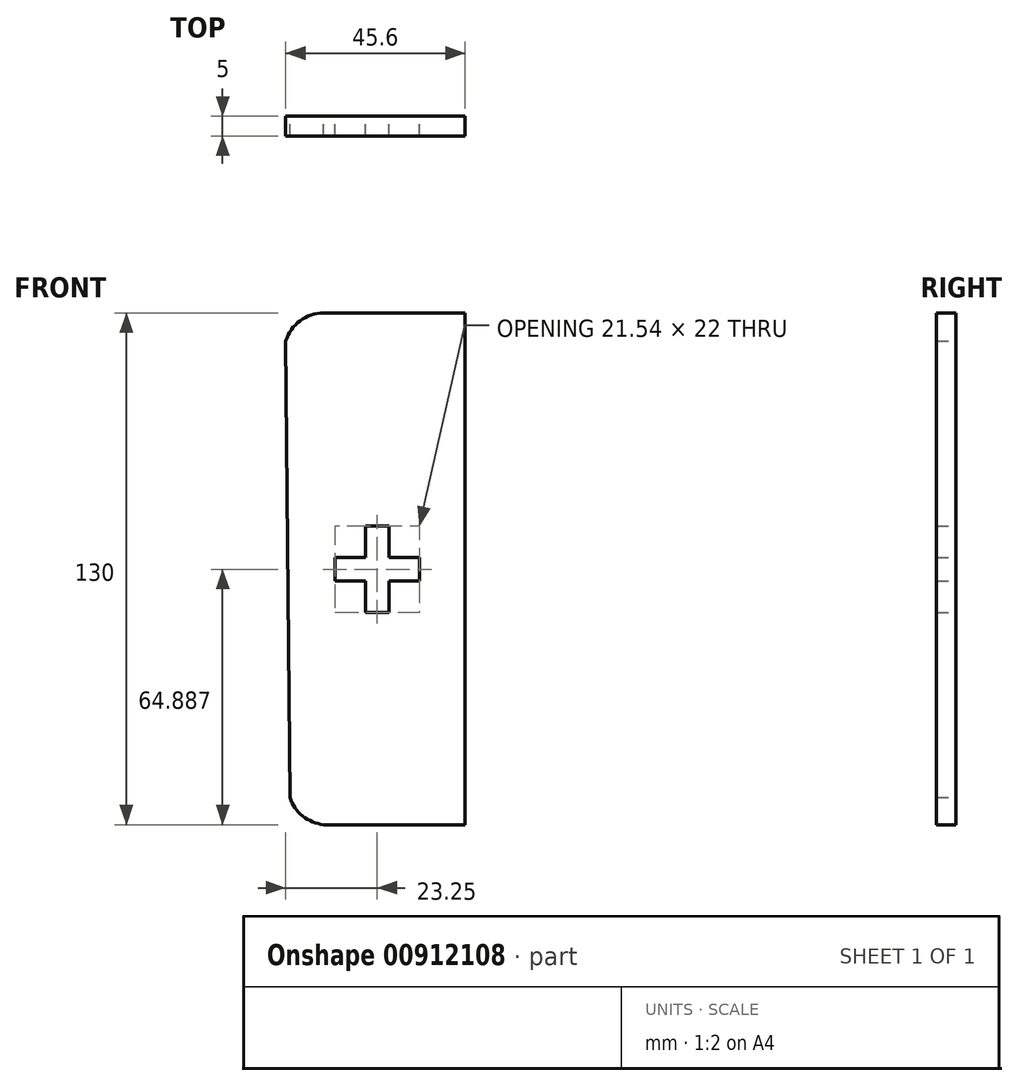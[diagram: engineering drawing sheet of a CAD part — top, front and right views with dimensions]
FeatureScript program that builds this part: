
annotation { "Feature Type Name" : "Feature", "Feature Type Description" : "" }
export const myFeature = defineFeature(function(context is Context, id is Id, definition is map)
    precondition{}
    {
        {
            var Q0;
            Q0=qCreatedBy(makeId("Front.planeOp"),FACE);
            var sketch = newSketch(context, id + "F0", { "sketchPlane" : qUnion([Q0])});
            skLineSegment(sketch, "E0", {"start": v(8.34, 35.26) * mm, "end": v(-27.63, 35.26) * mm});
            skArc(sketch, "E1", {"start": v(-27.63, 35.26) * mm, "mid": v(-33.63, 33.28) * mm, "end": v(-37.26, 28.1) * mm});
            skLineSegment(sketch, "E2", {"start": v(-27.63, -94.74) * mm, "end": v(8.34, -94.74) * mm});
            skArc(sketch, "E3", {"start": v(-36.18, -87.81) * mm, "mid": v(-32.94, -92.55) * mm, "end": v(-27.63, -94.74) * mm});
            skLineSegment(sketch, "E4", {"start": v(-37.26, 28.1) * mm, "end": v(-36.18, -87.81) * mm});
            skLineSegment(sketch, "E5", {"start": v(8.34, 35.26) * mm, "end": v(8.34, -94.74) * mm});
            skPoint(sketch, "E6.endSnap0", {"position": v(8.34, -29.74) * mm});
            skLineSegment(sketch, "E7.top", {"start": v(-17, -18.85) * mm, "end": v(-11, -18.85) * mm});
            skLineSegment(sketch, "E7.left", {"start": v(-17, -26.85) * mm, "end": v(-17, -18.85) * mm});
            skLineSegment(sketch, "E7.right", {"start": v(-11, -26.85) * mm, "end": v(-11, -18.85) * mm});
            skLineSegment(sketch, "E8.top", {"start": v(-11, -40.85) * mm, "end": v(-17, -40.85) * mm});
            skLineSegment(sketch, "E8.left", {"start": v(-11, -32.85) * mm, "end": v(-11, -40.85) * mm});
            skLineSegment(sketch, "E8.right", {"start": v(-17, -32.85) * mm, "end": v(-17, -40.85) * mm});
            skPoint(sketch, "E9", {"position": v(-11, -26.85) * mm});
            skPoint(sketch, "E10", {"position": v(-11, -32.85) * mm});
            skLineSegment(sketch, "E11.bottom", {"start": v(-11, -26.85) * mm, "end": v(-3.24, -26.85) * mm});
            skLineSegment(sketch, "E11.top", {"start": v(-11, -32.85) * mm, "end": v(-3.24, -32.85) * mm});
            skLineSegment(sketch, "E11.right", {"start": v(-3.24, -26.85) * mm, "end": v(-3.24, -32.85) * mm});
            skLineSegment(sketch, "E12.bottom", {"start": v(-17, -32.85) * mm, "end": v(-24.78, -32.85) * mm});
            skLineSegment(sketch, "E12.top", {"start": v(-17, -26.85) * mm, "end": v(-24.78, -26.85) * mm});
            skLineSegment(sketch, "E12.right", {"start": v(-24.78, -32.85) * mm, "end": v(-24.78, -26.85) * mm});
            skPoint(sketch, "E13.trimOffspring.end.orphan", {"position": v(8.34, -28.3) * mm});
            skPoint(sketch, "E6.start.orphan", {"position": v(-36.72, -29.85) * mm});
            skSolve(sketch);
        }
        {
            var Q0;
            Q0=makeQuery(id+"F0.imprint","IMPRINT",FACE,{"disambiguationData":[TD([[makeQuery(id+"F0.imprint","IMPRINT",EDGE,{"derivedFrom":sQuery(id+"F0.wireOp",EDGE,"E0")}),1.0]])]});
            extrude(context, id + "F1", {"entities" : qUnion([Q0]), "depth" : 5 * mm, "offsetDistance" : 25 * mm});
        }
    });
